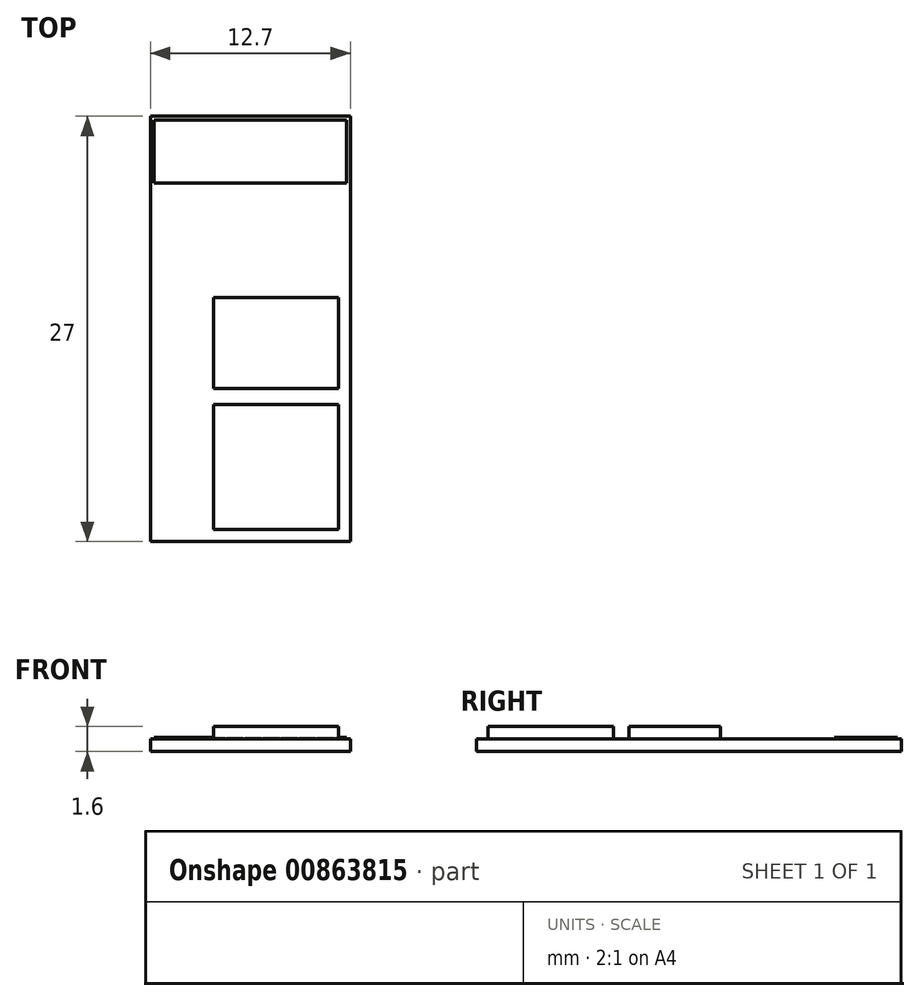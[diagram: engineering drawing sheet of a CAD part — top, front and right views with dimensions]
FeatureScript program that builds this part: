
annotation { "Feature Type Name" : "Feature", "Feature Type Description" : "" }
export const myFeature = defineFeature(function(context is Context, id is Id, definition is map)
    precondition{}
    {
        {
            var Q0;
            Q0=qCreatedBy(makeId("Top.planeOp"),FACE);
            var sketch = newSketch(context, id + "F0", { "sketchPlane" : qUnion([Q0])});
            skLineSegment(sketch, "E0.bottom", {"start": v(0, 0) * mm, "end": v(12.7, 0) * mm});
            skLineSegment(sketch, "E0.top", {"start": v(0, 27) * mm, "end": v(12.7, 27) * mm});
            skLineSegment(sketch, "E0.left", {"start": v(0, 0) * mm, "end": v(0, 27) * mm});
            skLineSegment(sketch, "E0.right", {"start": v(12.7, 0) * mm, "end": v(12.7, 27) * mm});
            skSolve(sketch);
        }
        {
            var Q0;
            Q0 = qSketchRegion(id + "F0", true);
            extrude(context, id + "F1", {"entities" : qUnion([Q0]), "depth" : .8 * mm, "offsetDistance" : 25 * mm});
        }
        {
            var Q0;
            Q0=makeQuery(id+"F1.opExtrude","CAP_FACE",FACE,{"disambiguationData":[OSD([sQuery(id+"F0.wireOp",EDGE,"E0.bottom"),sQuery(id+"F0.wireOp",EDGE,"E0.top"),sQuery(id+"F0.wireOp",EDGE,"E0.left"),sQuery(id+"F0.wireOp",EDGE,"E0.right")])],"isStart":false});
            var sketch = newSketch(context, id + "F2", { "sketchPlane" : qUnion([Q0])});
            skLineSegment(sketch, "E1.bottom", {"start": v(11.95, 0.75) * mm, "end": v(4, 0.75) * mm});
            skLineSegment(sketch, "E1.top", {"start": v(11.95, 8.7) * mm, "end": v(4, 8.7) * mm});
            skLineSegment(sketch, "E1.left", {"start": v(11.95, 0.75) * mm, "end": v(11.95, 8.7) * mm});
            skLineSegment(sketch, "E1.right", {"start": v(4, 0.75) * mm, "end": v(4, 8.7) * mm});
            skLineSegment(sketch, "E2.bottom", {"start": v(11.95, 9.7) * mm, "end": v(4, 9.7) * mm});
            skLineSegment(sketch, "E2.top", {"start": v(11.95, 15.5) * mm, "end": v(4, 15.5) * mm});
            skLineSegment(sketch, "E2.left", {"start": v(11.95, 9.7) * mm, "end": v(11.95, 15.5) * mm});
            skLineSegment(sketch, "E2.right", {"start": v(4, 9.7) * mm, "end": v(4, 15.5) * mm});
            skSolve(sketch);
        }
        {
            var Q0;
            Q0 = qSketchRegion(id + "F2", true);
            extrude(context, id + "F3", {"entities" : qUnion([Q0]), "depth" : .8 * mm, "offsetDistance" : 25 * mm});
        }
        {
            var Q0;
            Q0=makeQuery(id+"F1.opExtrude","CAP_FACE",FACE,{"disambiguationData":[OSD([sQuery(id+"F0.wireOp",EDGE,"E0.bottom"),sQuery(id+"F0.wireOp",EDGE,"E0.top"),sQuery(id+"F0.wireOp",EDGE,"E0.left"),sQuery(id+"F0.wireOp",EDGE,"E0.right")])],"isStart":false});
            var sketch = newSketch(context, id + "F4", { "sketchPlane" : qUnion([Q0])});
            skLineSegment(sketch, "E3.bottom", {"start": v(0.25, 26.75) * mm, "end": v(12.45, 26.75) * mm});
            skLineSegment(sketch, "E3.top", {"start": v(0.25, 22.75) * mm, "end": v(12.45, 22.75) * mm});
            skLineSegment(sketch, "E3.left", {"start": v(0.25, 26.75) * mm, "end": v(0.25, 22.75) * mm});
            skLineSegment(sketch, "E3.right", {"start": v(12.45, 26.75) * mm, "end": v(12.45, 22.75) * mm});
            skSolve(sketch);
        }
        {
            var Q0;
            Q0 = qSketchRegion(id + "F4", true);
            extrude(context, id + "F5", {"entities" : qUnion([Q0]), "depth" : .1 * mm, "offsetDistance" : 25 * mm});
        }
    });
